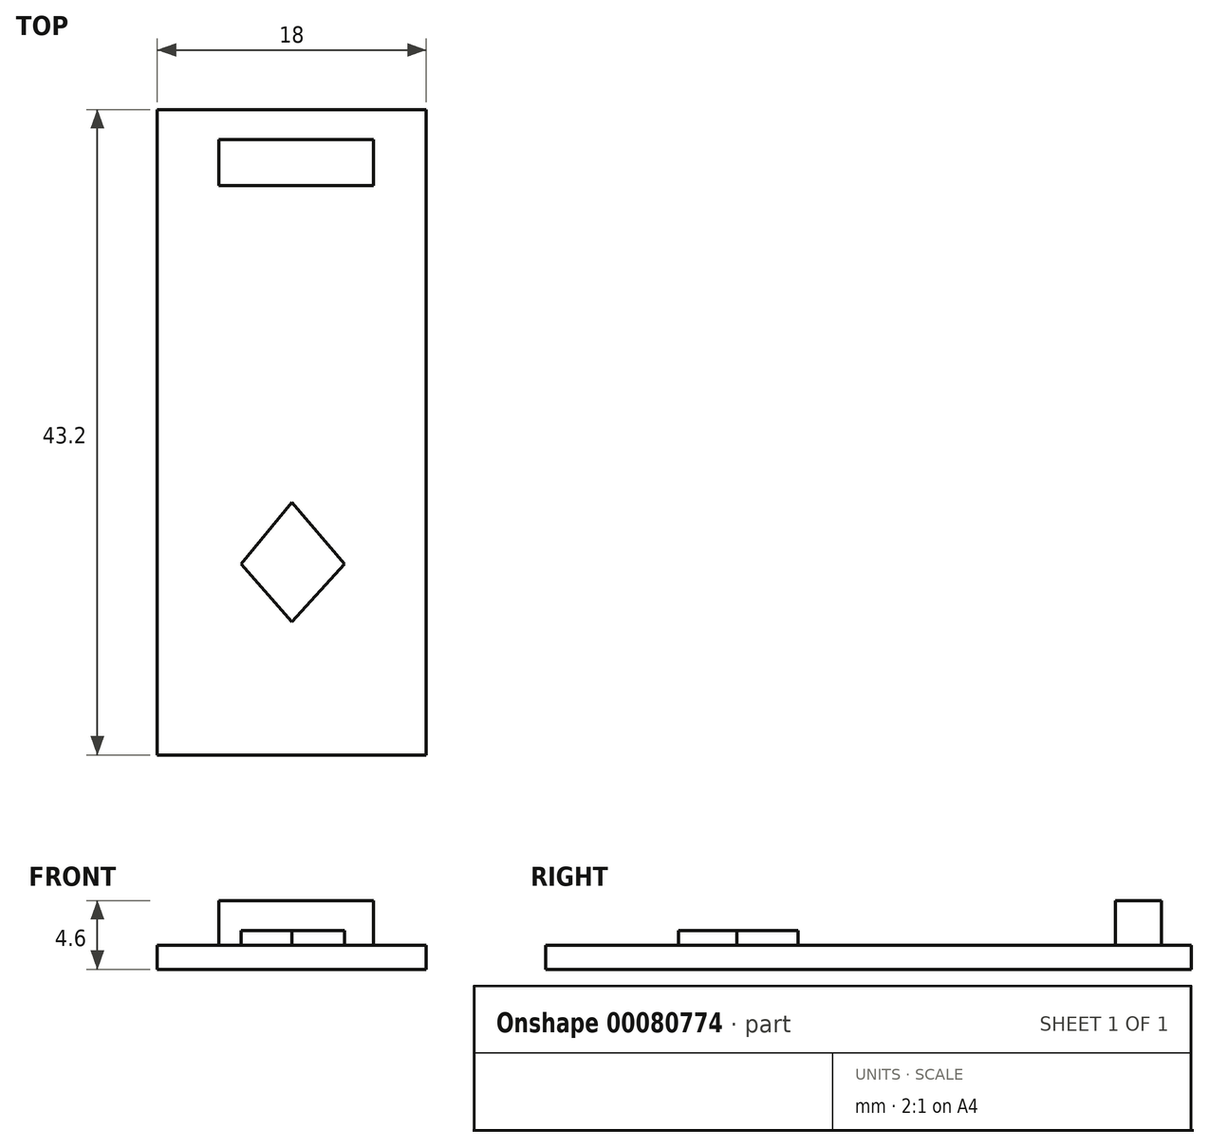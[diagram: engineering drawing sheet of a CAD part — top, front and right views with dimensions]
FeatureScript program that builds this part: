
annotation { "Feature Type Name" : "Feature", "Feature Type Description" : "" }
export const myFeature = defineFeature(function(context is Context, id is Id, definition is map)
    precondition{}
    {
        {
            var Q0;
            Q0=qCreatedBy(makeId("Top.planeOp"),FACE);
            var sketch = newSketch(context, id + "F0", { "sketchPlane" : qUnion([Q0])});
            skLineSegment(sketch, "E0.bottom", {"start": v(-9, 20.56) * mm, "end": v(9, 20.56) * mm});
            skLineSegment(sketch, "E0.top", {"start": v(-9, -22.64) * mm, "end": v(9, -22.64) * mm});
            skLineSegment(sketch, "E0.left", {"start": v(-9, 20.56) * mm, "end": v(-9, -22.64) * mm});
            skLineSegment(sketch, "E0.right", {"start": v(9, 20.56) * mm, "end": v(9, -22.64) * mm});
            skPoint(sketch, "E0.middle", {"position": v(0, -1.04) * mm});
            skSolve(sketch);
        }
        {
            var Q0;
            Q0=makeQuery(id+"F0.imprint","IMPRINT",FACE,{"disambiguationData":[TD([[makeQuery(id+"F0.imprint","IMPRINT",EDGE,{"derivedFrom":sQuery(id+"F0.wireOp",EDGE,"E0.bottom")}),-1.0]])]});
            extrude(context, id + "F1", {"entities" : qUnion([Q0]), "depth" : 1.6 * mm});
        }
        {
            var Q0;
            Q0=makeQuery(id+"F1.opExtrude","CAP_FACE",FACE,{"disambiguationData":[OSD([sQuery(id+"F0.wireOp",EDGE,"E0.bottom"),sQuery(id+"F0.wireOp",EDGE,"E0.top"),sQuery(id+"F0.wireOp",EDGE,"E0.left"),sQuery(id+"F0.wireOp",EDGE,"E0.right")])],"isStart":false});
            var sketch = newSketch(context, id + "F2", { "sketchPlane" : qUnion([Q0])});
            skLineSegment(sketch, "E1", {"start": v(0, -13.74) * mm, "end": v(-3.38, -9.86) * mm});
            skLineSegment(sketch, "E2", {"start": v(-3.38, -9.86) * mm, "end": v(0, -5.74) * mm});
            skLineSegment(sketch, "E3", {"start": v(0, -5.74) * mm, "end": v(3.52, -9.86) * mm});
            skLineSegment(sketch, "E4", {"start": v(3.52, -9.86) * mm, "end": v(0, -13.74) * mm});
            skLineSegment(sketch, "E5.bottom", {"start": v(-4.88, 18.55) * mm, "end": v(5.47, 18.55) * mm});
            skLineSegment(sketch, "E5.top", {"start": v(-4.88, 15.5) * mm, "end": v(5.47, 15.5) * mm});
            skLineSegment(sketch, "E5.left", {"start": v(-4.88, 18.55) * mm, "end": v(-4.88, 15.5) * mm});
            skLineSegment(sketch, "E5.right", {"start": v(5.47, 18.55) * mm, "end": v(5.47, 15.5) * mm});
            skSolve(sketch);
        }
        {
            var Q0;
            Q0=makeQuery(id+"F2.imprint","IMPRINT",FACE,{"disambiguationData":[TD([[makeQuery(id+"F2.imprint","IMPRINT",EDGE,{"derivedFrom":sQuery(id+"F2.wireOp",EDGE,"E1")}),-1.0]])]});
            extrude(context, id + "F3", {"entities" : qUnion([Q0]), "operationType" : NewBodyOperationType.ADD, "depth" : 1 * mm});
        }
        {
            var Q0;
            Q0=makeQuery(id+"F2.imprint","IMPRINT",FACE,{"disambiguationData":[TD([[makeQuery(id+"F2.imprint","IMPRINT",EDGE,{"derivedFrom":sQuery(id+"F2.wireOp",EDGE,"E5.bottom")}),-1.0]])]});
            extrude(context, id + "F4", {"entities" : qUnion([Q0]), "operationType" : NewBodyOperationType.ADD, "depth" : 3 * mm});
        }
    });
